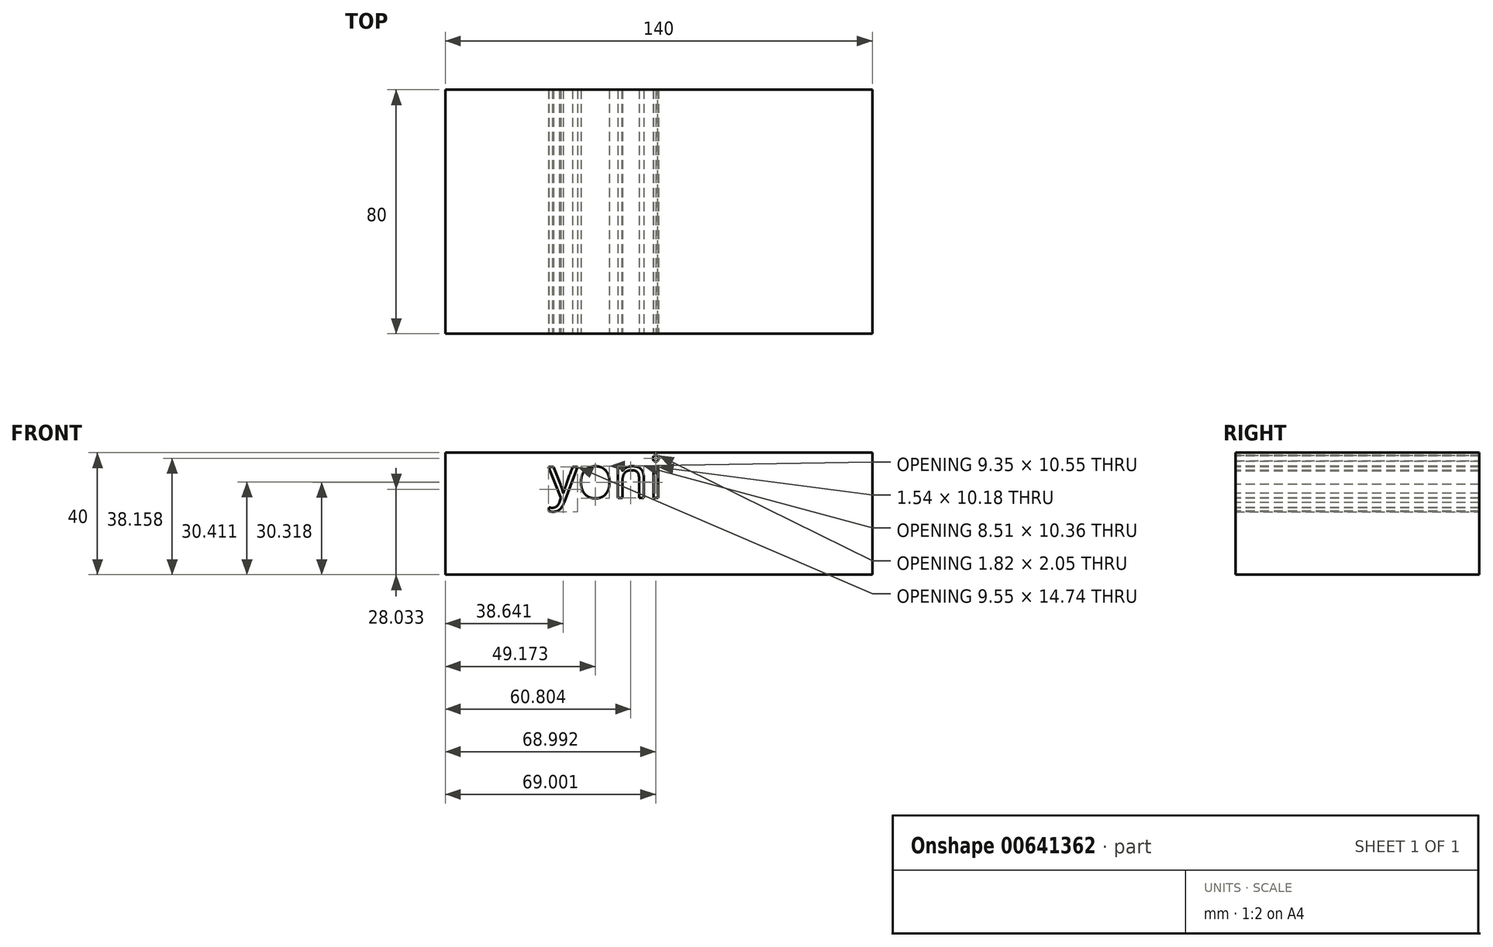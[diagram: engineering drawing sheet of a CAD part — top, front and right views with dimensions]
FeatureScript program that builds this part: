
annotation { "Feature Type Name" : "Feature", "Feature Type Description" : "" }
export const myFeature = defineFeature(function(context is Context, id is Id, definition is map)
    precondition{}
    {
        {
            var Q0;
            Q0=qCreatedBy(makeId("Top.planeOp"),FACE);
            var sketch = newSketch(context, id + "F0", { "sketchPlane" : qUnion([Q0])});
            skLineSegment(sketch, "E0.rect.bottom", {"start": v(-70, -40) * mm, "end": v(70, -40) * mm});
            skLineSegment(sketch, "E0.rect.top", {"start": v(-70, 40) * mm, "end": v(70, 40) * mm});
            skLineSegment(sketch, "E0.rect.left", {"start": v(-70, -40) * mm, "end": v(-70, 40) * mm});
            skLineSegment(sketch, "E0.rect.right", {"start": v(70, -40) * mm, "end": v(70, 40) * mm});
            skPoint(sketch, "E0.rect.middle", {"position": v(0, 0) * mm});
            skSolve(sketch);
        }
        {
            var Q0;
            Q0=makeQuery(id+"F0.imprint","IMPRINT",FACE,{"disambiguationData":[TD([[makeQuery(id+"F0.imprint","IMPRINT",EDGE,{"derivedFrom":sQuery(id+"F0.wireOp",EDGE,"E0.rect.bottom")}),1.0]])]});
            extrude(context, id + "F1", {"entities" : qUnion([Q0]), "depth" : 40 * mm});
        }
        {
            var Q0;
            Q0=makeQuery(id+"F1.opExtrude","SWEPT_FACE",FACE,{"disambiguationData":[OSD([sQuery(id+"F0.wireOp",EDGE,"E0.rect.bottom")])]});
            var sketch = newSketch(context, id + "F2", { "sketchPlane" : qUnion([Q0])});
            skText(sketch, "E1", { "text": "yoni\n", "fontName": "OpenSans-Regular.ttf"});
            const initialGuessF2  = {"E1": [-0.03615, 0.02523, 1, 0, 0.01369]};
            skSetInitialGuess(sketch, initialGuessF2);
            skSolve(sketch);
        }
        {
            var Q0;
            Q0=qSketchRegion(id+"F2",true);
            extrude(context, id + "F3", {"entities" : qUnion([Q0]), "operationType" : NewBodyOperationType.REMOVE, "oppositeDirection" : true, "depth" : 10000 * mm, "symmetric" : true});
        }
        {
            var Q0;
            Q0=makeQuery(id+"F3.boolean.opBoolean","SPLIT",FACE,{"disambiguationData":[TD([makeQuery(id+"F3.opExtrude","SWEPT_FACE",FACE,{"disambiguationData":[OSD([sQuery(id+"F2.wireOp",EDGE,"E1.sketch_text.stroke-25")])]})])],"derivedFrom":makeQuery(id+"F1.opExtrude","SWEPT_FACE",FACE,{"disambiguationData":[OSD([sQuery(id+"F0.wireOp",EDGE,"E0.rect.bottom")])]})});
            extrude(context, id + "F4", {"entities" : qUnion([Q0]), "operationType" : NewBodyOperationType.REMOVE, "endBound" : BoundingType.THROUGH_ALL, "oppositeDirection" : true, "depth" : 25 * mm});
        }
    });
